# Revit family: QF_MOFFAT WALDORF_SN8100E
name_source: partatom
category: Specialty Equipment
revit_build: Autodesk Revit Architecture 2012 (Build: 20110916_2132(x64)
units: mm (PartAtom-declared; Revit-internal decimal feet)

## types (1)
- QF_MOFFAT WALDORF_SN8100E
    Apparent Power = 0 VA
    Body Finish = QF_Finishes_Stainless Steel
    Conn Conduit = Yes
    Cycle = 50 Hz
    Depth = 510 mm  [stored 1.67323 ft]
    Description = ELECTRIC SALAMANDER
    Elec Conn Connection Height = 0 mm  [stored 0 ft]
    Elec Conn RI Height = 0 mm  [stored 0 ft]
    FL Amps = 15 A
    Height = 514 mm  [stored 1.68635 ft]
    Manufacturer = MOFFAT WALDORF
    Max Overcurrent Protection = 0 A
    Min Ckt Ampacity = 0 A
    Model = SN8100E
    Number of Poles = 1
    Phase = 1
    URL = www.moffat.com
    URL Cutsheet = www.moffat.com
    Volts = 240 V
    Watts = 3600 W
    Weight in Pounds = 53
    Width = 600 mm  [stored 1.9685 ft]

note: [stored X ft] marks values corroborated as IEEE doubles in the binary element streams (Revit-internal decimal feet)

## geometry (parser evidence)
native form markers: Blend x4, Sweep x4
no freeform markers — native parametric forms only
